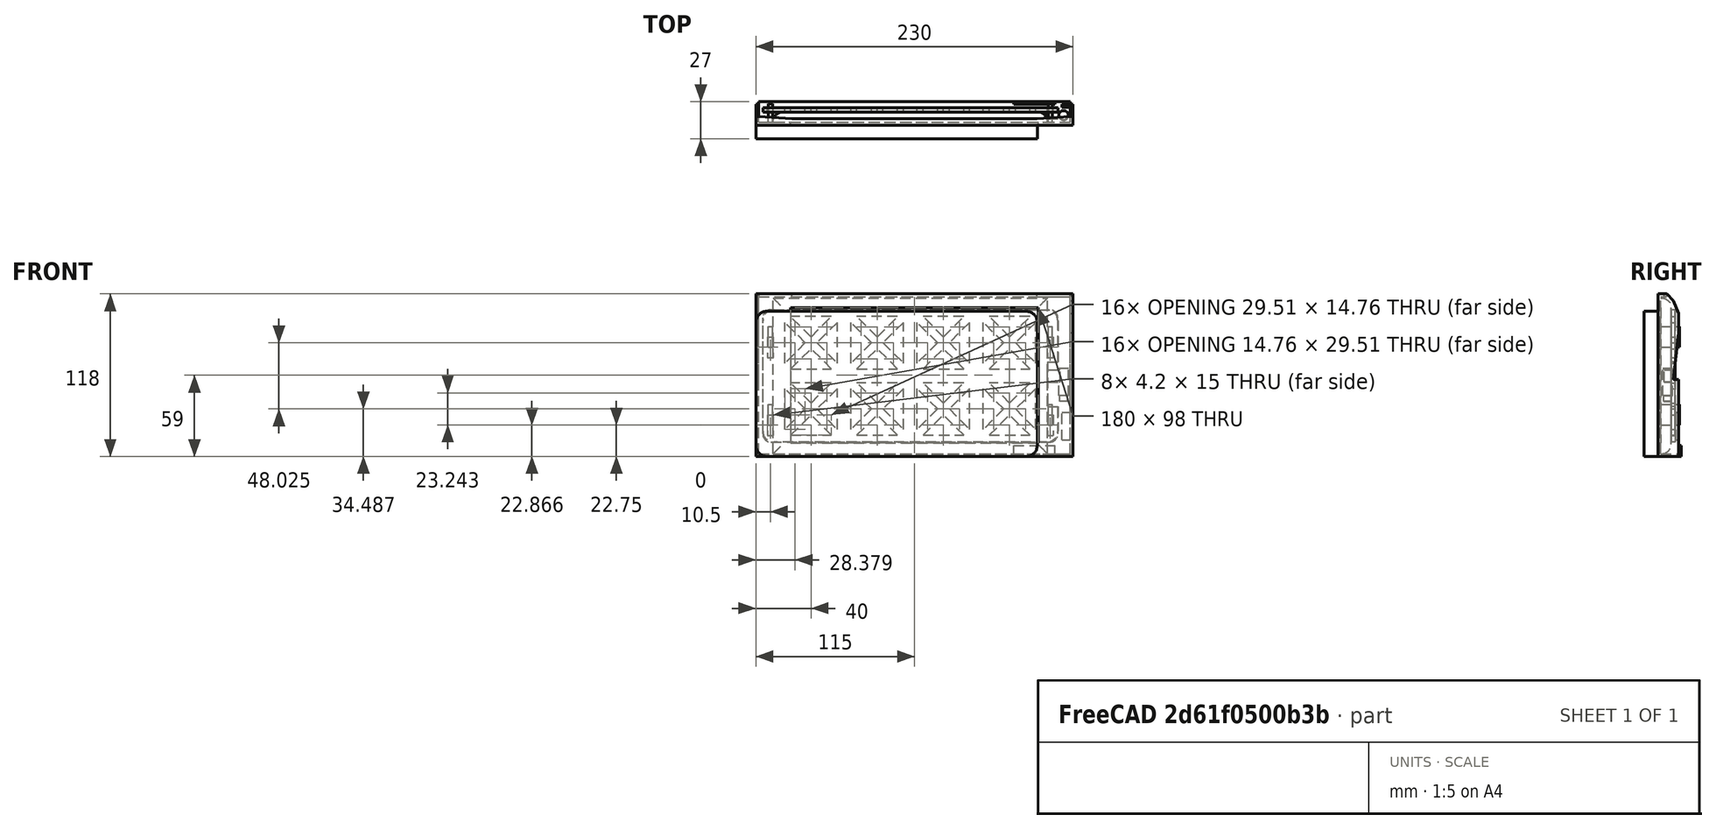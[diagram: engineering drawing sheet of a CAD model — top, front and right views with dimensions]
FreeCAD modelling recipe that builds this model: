
FCSTD DOCUMENT  (FreeCAD 0.18.1R)
Label: case
License: All rights reserved
LicenseURL: http://en.wikipedia.org/wiki/All_rights_reserved
objects: Part::Box×15, Part::Cut×15, Sketcher::SketchObject×7, Part::Extrusion×4, Mesh::Feature×3, Part::Cylinder×2, Part::MultiFuse×2, Part::Fillet×2, PartDesign::LinearPattern×2, App::DocumentObjectGroup×2, Spreadsheet::Sheet×1, PartDesign::Pad×1, PartDesign::Pocket×1, PartDesign::MultiTransform×1, PartDesign::Body×1, Image::ImagePlane×1
note: 55 computed .brp shape members not serialized (recipe doc carries the construction recipe); baked Part::Feature solids carry a one-line shape summary decoded from their .brp

FEATURE [Part::Box] Box  label="Cube"
  AttacherType = Attacher::AttachEngine3D
  Height = 118
  Length = 226
  Placement = pos=(2,0,0) rot=(0,0,1;0rad)
  Width = 2
  expr: Placement.Rotation.Axis.x = 0
  expr: Length = Spreadsheet.avl_width - Spreadsheet.thickness * 2
  expr: Placement.Base.x = Spreadsheet.thickness
  expr: Height = Spreadsheet.thickness * 2 + Spreadsheet.tablet_height + Spreadsheet.tablet_height_margin
  expr: Width = Spreadsheet.thickness
FEATURE [Part::Box] Box001  label="Cube001"
  AttacherType = Attacher::AttachEngine3D
  Height = 98
  Length = 180
  Placement = pos=(25,-17,10) rot=(0,0,1;0rad)
  Width = 34
  expr: Placement.Base.y = -Cube001.Width / 2
  expr: Placement.Base.x = Spreadsheet.case_sides_width
  expr: Placement.Base.z = Spreadsheet.case_bottom_height
  expr: Height = Spreadsheet.thickness * 2 + Spreadsheet.tablet_height + Spreadsheet.tablet_height_margin - Spreadsheet.case_bottom_height - Spreadsheet.case_top_height
  expr: Width = Spreadsheet.case_bottom_depth * 2
  expr: Length = Spreadsheet.avl_width - Spreadsheet.case_sides_width * 2
FEATURE [Part::Cut] Cut  label="Main Frame"
  Base = -> Box
  Tool = -> Box001
FEATURE [Sketcher::SketchObject] Sketch
  MapMode = 2
  Support = -> [Sketch]
  sketch-geometry (6):
    g0: LineSegment StartX=0 StartY=0 StartZ=0 EndX=0 EndY=6.3 EndZ=0
    g1: LineSegment StartX=0 StartY=6.3 StartZ=0 EndX=26 EndY=4.5 EndZ=0
    g2: LineSegment StartX=26 StartY=4.5 StartZ=0 EndX=204 EndY=4.5 EndZ=0
    g3: LineSegment StartX=204 StartY=4.5 StartZ=0 EndX=230 EndY=6.3 EndZ=0
    g4: LineSegment StartX=230 StartY=6.3 StartZ=0 EndX=230 EndY=0 EndZ=0
    g5: LineSegment StartX=230 StartY=0 StartZ=0 EndX=0 EndY=0 EndZ=0
  constraints (18):
    c: PointOnObject(g0,g-1)
    c: Vertical(g0)
    c: Coincident(g0,g1)
    c: Coincident(g1,g2)
    c: Horizontal(g2)
    c: Coincident(g2,g3)
    c: Coincident(g3,g4)
    c: PointOnObject(g4,g-1)
    c: Vertical(g4)
    c: Coincident(g4,g5)
    c: Coincident(g5,g0)
    c: Coincident(g0,g-1)
    c: DistanceX(g5,g5) = 230
    c: DistanceY(g0,g0) = 6.3
    c: Equal(g4,g0)
    c: DistanceX(g2,g3) = 26
    c: DistanceX(g0,g1) = 26
    c: DistanceY(g-1,g1) = 4.5
FEATURE [Part::Extrusion] Extrude  label="Top Thin Beam"
  Base = -> Sketch
  Dir = (0,0,1)
  DirMode = 2
  FaceMakerClass = Part::FaceMakerBullseye
  LengthFwd = 2
  LengthRev = 0
  Placement = pos=(0,0,116) rot=(0,0,1;0rad)
  Solid = true
  Symmetric = false
  expr: LengthFwd = Spreadsheet.thickness
  expr: Placement.Base.z = Spreadsheet.thickness + Spreadsheet.tablet_height + Spreadsheet.tablet_height_margin
FEATURE [Sketcher::SketchObject] Sketch001
  MapMode = 4
  Placement = pos=(0,0,0) rot=(0.57735,0.57735,0.57735;2.0944rad)
  expr: Constraints[15] = Spreadsheet.case_sides_depth
  expr: Constraints[10] = Spreadsheet.case_sides_depth
  expr: Constraints.Height = Spreadsheet.thickness * 2 + Spreadsheet.tablet_height + Spreadsheet.tablet_height_margin
  sketch-geometry (9):
    g0: LineSegment StartX=0 StartY=0 StartZ=0 EndX=15 EndY=0 EndZ=0
    g1: LineSegment StartX=15 StartY=0 StartZ=0 EndX=15 EndY=56 EndZ=0
    g2: LineSegment StartX=15 StartY=56 StartZ=0 EndX=11 EndY=56 EndZ=0
    g3: LineSegment StartX=11 StartY=56 StartZ=0 EndX=15 EndY=90 EndZ=0
    g4: LineSegment StartX=15 StartY=90 StartZ=0 EndX=15 EndY=104 EndZ=0
    g5: LineSegment StartX=15 StartY=104 StartZ=0 EndX=11 EndY=113 EndZ=0
    g6: LineSegment StartX=11 StartY=113 StartZ=0 EndX=6.3 EndY=118 EndZ=0
    g7: LineSegment StartX=0 StartY=118 StartZ=0 EndX=0 EndY=0 EndZ=0
    g8: LineSegment StartX=0 StartY=118 StartZ=0 EndX=6.3 EndY=118 EndZ=0
  constraints (26):
    c: Coincident(g8,g7)
    c: Coincident(g8,g6)
    c: Coincident(g6,g5)
    c: Coincident(g5,g4)
    c: Coincident(g4,g3)
    c: Coincident(g2,g3)
    c: Coincident(g2,g1)
    c: Coincident(g0,g1)
    c: Coincident(g0,g-1)
    c: Horizontal(g0)
    c: DistanceX(g0,g0) = 15
    c: Vertical(g1)
    c: DistanceY(g1,g1) = 56
    c: Horizontal(g2)
    c: DistanceX(g2,g2) = 4
    c: DistanceX(g-1,g3) = 15
    c: DistanceY(g-1,g3) = 90
    c: Vertical(g4)
    c: DistanceY(g-1,g4) = 104
    c: DistanceX(g-1,g5) = 11
    c: DistanceY(g-1,g5) = 113
    c: Coincident(g7,g-1)
    c: Vertical(g7)
    c: DistanceY(g7,g7) = 118  'Height'
    c: Horizontal(g8)
    c: DistanceX(g8,g8) = 6.3
FEATURE [Part::Extrusion] Extrude001  label="RightVerticalContour"
  Base = -> Sketch001
  Dir = (1,0,0)
  DirMode = 2
  FaceMakerClass = Part::FaceMakerBullseye
  LengthFwd = 2
  LengthRev = 0
  Placement = pos=(228,0,0) rot=(0,0,1;0rad)
  Solid = true
  Symmetric = false
  expr: LengthFwd = Spreadsheet.B1
  expr: Placement.Base.x = Spreadsheet.B2 - Spreadsheet.B1
FEATURE [Sketcher::SketchObject] Sketch002
  MapMode = 4
  Placement = pos=(0,0,0) rot=(0.57735,0.57735,0.57735;2.0944rad)
  expr: Constraints[15] = Spreadsheet.case_sides_depth
  expr: Constraints[10] = Spreadsheet.case_sides_depth
  expr: Constraints.Height = Sketch001.Constraints.Height
  sketch-geometry (9):
    g0: LineSegment StartX=0 StartY=0 StartZ=0 EndX=15 EndY=0 EndZ=0
    g1: LineSegment StartX=15 StartY=0 StartZ=0 EndX=15 EndY=56 EndZ=0
    g2: LineSegment StartX=15 StartY=56 StartZ=0 EndX=11 EndY=56 EndZ=0
    g3: LineSegment StartX=11 StartY=56 StartZ=0 EndX=15 EndY=90 EndZ=0
    g4: LineSegment StartX=15 StartY=90 StartZ=0 EndX=15 EndY=104 EndZ=0
    g5: LineSegment StartX=15 StartY=104 StartZ=0 EndX=11 EndY=113 EndZ=0
    g6: LineSegment StartX=11 StartY=113 StartZ=0 EndX=6.3 EndY=118 EndZ=0
    g7: LineSegment StartX=0 StartY=118 StartZ=0 EndX=0 EndY=0 EndZ=0
    g8: LineSegment StartX=0 StartY=118 StartZ=0 EndX=6.3 EndY=118 EndZ=0
  constraints (26):
    c: Coincident(g8,g7)
    c: Coincident(g8,g6)
    c: Coincident(g6,g5)
    c: Coincident(g5,g4)
    c: Coincident(g4,g3)
    c: Coincident(g2,g3)
    c: Coincident(g2,g1)
    c: Coincident(g0,g1)
    c: Coincident(g0,g-1)
    c: Horizontal(g0)
    c: DistanceX(g0,g0) = 15
    c: Vertical(g1)
    c: DistanceY(g1,g1) = 56
    c: Horizontal(g2)
    c: DistanceX(g2,g2) = 4
    c: DistanceX(g-1,g3) = 15
    c: DistanceY(g-1,g3) = 90
    c: Vertical(g4)
    c: DistanceY(g-1,g4) = 104
    c: DistanceX(g-1,g5) = 11
    c: DistanceY(g-1,g5) = 113
    c: Coincident(g7,g-1)
    c: Vertical(g7)
    c: DistanceY(g7,g7) = 118  'Height'
    c: Horizontal(g8)
    c: DistanceX(g8,g8) = 6.3
FEATURE [Part::Extrusion] Extrude002  label="LefttVerticalContour"
  Base = -> Sketch002
  Dir = (1,0,0)
  DirMode = 2
  FaceMakerClass = Part::FaceMakerBullseye
  LengthFwd = 2
  LengthRev = 0
  Solid = true
  Symmetric = false
  expr: LengthFwd = Spreadsheet.thickness
FEATURE [Part::Box] Box009  label="Bottom"
  AttacherType = Attacher::AttachEngine3D
  Height = 2
  Length = 226
  Placement = pos=(2,0,0) rot=(0,0,1;0rad)
  Width = 17
  expr: Width = Spreadsheet.case_bottom_depth
  expr: Placement.Base.x = Spreadsheet.thickness
  expr: Height = Spreadsheet.thickness
  expr: Length = Spreadsheet.avl_width - Spreadsheet.thickness * 2
FEATURE [Part::Box] Box010  label="base"
  AttacherType = Attacher::AttachEngine3D
  Height = 15
  Length = 3
  Width = 13.5
  expr: Height = Spreadsheet.back_support_height
  expr: Width = Spreadsheet.tablet_thickness + Spreadsheet.back_thickness * 2
  expr: Length = Spreadsheet.back_support_thickness
FEATURE [Spreadsheet::Sheet] Spreadsheet
  cells = A1=thickness; B1(thickness)=2; A2=avl_width; B2(avl_width)=230; A3=tablet_height_margin; B3(tablet_height_margin)=1; A4=tablet_height; B4(tablet_height)=113; A5=tablet_length_margin; B5(tablet_length_margin)=0.5; A6=tablet_length; B6(tablet_length)=199; A7=tablet_thickness; B7(tablet_thickness)=7.5; A8=usb_length; B8(usb_length)=15; A9=back_support_height; B9(back_support_height)=15; A10=back_support_thickness; B10(back_support_thickness)=3; A11=back_height_rel_tablet; B11(back_height_rel_tablet)=0.85; A12=back_thickness; B12(back_thickness)=3; A13=case_sides_depth; B13(case_sides_depth)=15; A14=case_bottom_depth; B14(case_bottom_depth)=17; A15=case_sides_width; B15(case_sides_width)=25; A16=case_bottom_height; B16(case_bottom_height)=10; A17=case_top_height; B17(case_top_height)=10; A18=back_width_offset; B18(back_width_offset)=4; A19=back_corner_radius; B19(back_corner_radius)=8; A20=back_pattern_beam_thickness; B20(back_pattern_beam_thickness)=6; A21=back_pattern_size; B21(back_pattern_size)=44; A22=back_support_opening_inside_margin; B22(back_support_opening_inside_margin)=4; A23=back_pattern_hor_num; B23(back_pattern_hor_num)=4; A24=back_pattern_ver_num; B24(back_pattern_ver_num)=2; A25=back_pattern_linear_pattern_length; B25(back_pattern_linear_pattern_length)==back_length - 2 * (back_support_thickness + back_support_opening_inside_margin + back_width_offset) - back_pattern_size - (back_length - 2 * (back_support_thickness + back_support_opening_inside_margin + back_width_offset) - back_pattern_hor_num * back_pattern_size) / back_pattern_hor_num; A26=back_length; B26(back_length)==Spreadsheet.tablet_length + 2 * Spreadsheet.tablet_length_margin + 2 * Spreadsheet.back_support_thickness + 2 * Spreadsheet.back_width_offset; A27=magnet_width; B27(magnet_width)=6; A28=magnet_length; B28(magnet_length)=8; A29=magnet_thickness; B29(magnet_thickness)=3; A30=back_support_opening_factor; B30(back_support_opening_factor)=1.4
FEATURE [Part::Box] Box011  label="Tablet"
  AttacherType = Attacher::AttachEngine3D
  Height = 113
  Length = 199
  Placement = pos=(12.5,2,2) rot=(0,0,1;0rad)
  Width = 7.5
  expr: Placement.Base.y = Spreadsheet.thickness
  expr: Placement.Base.z = Spreadsheet.thickness
  expr: Height = Spreadsheet.tablet_height
  expr: Width = Spreadsheet.tablet_thickness
  expr: Length = Spreadsheet.tablet_length
FEATURE [Part::Cylinder] Cylinder
  Angle = 360
  AttacherType = Attacher::AttachEngine3D
  Height = 20
  Placement = pos=(11.75,2.5,-10) rot=(0,0,1;0rad)
  Radius = 3.5
  expr: Placement.Base.z = Cube010.Placement.Base.z - Cylinder.Height / 2
  expr: Placement.Base.y = Cube010.Placement.Base.y + Cube010.Width / 2
  expr: Placement.Base.x = Cube010.Placement.Base.x + Cube010.Length + Cylinder.Radius / 2
FEATURE [Part::Cylinder] Cylinder001
  Angle = 360
  AttacherType = Attacher::AttachEngine3D
  Height = 4
  Placement = pos=(11.75,2.5,-14) rot=(0,0,1;0rad)
  Radius = 3
  expr: Placement.Base.z = Cylinder.Placement.Base.z - Cylinder001.Height
  expr: Placement.Base.y = Cylinder.Placement.Base.y
  expr: Placement.Base.x = Cylinder.Placement.Base.x
FEATURE [Part::Box] Box012  label="Cube010"
  AttacherType = Attacher::AttachEngine3D
  Height = 9
  Length = 10
  Width = 5
FEATURE [Part::MultiFuse] Fusion001  label="USB"
  Placement = pos=(211.5,4.5,54) rot=(0,0,1;0rad)
  Shapes = -> [Cylinder,Box012,Cylinder001]
  expr: Placement.Base.y = Tablet.Placement.Base.y + Tablet.Width - Cube010.Width
  expr: Placement.Base.x = Tablet.Placement.Base.x + Tablet.Length
  expr: Placement.Base.z = Tablet.Placement.Base.z + Tablet.Height / 2 - Cube010.Height / 2
FEATURE [Part::Box] Box015  label="slot"
  AttacherType = Attacher::AttachEngine3D
  Height = 10
  Length = 10
  Placement = pos=(-3.5,7.5,7.5) rot=(0,0,1;0rad)
  Width = 3
  expr: Placement.Base.z = base.Placement.Base.z + base.Height / 2
  expr: Placement.Base.x = base.Placement.Base.x + base.Length / 2 - slot.Length / 2
  expr: Placement.Base.y = base.Placement.Base.y + Spreadsheet.tablet_thickness * 1mm
  expr: Width = Spreadsheet.back_thickness
FEATURE [Part::Cut] Cut001  label="TopLeftBackSupport"
  Base = -> Box010
  Placement = pos=(9,2,79.25) rot=(0,0,1;0rad)
  Tool = -> Box015
  expr: Placement.Base.y = Tablet.Placement.Base.y
  expr: Placement.Base.x = Tablet.Placement.Base.x - Spreadsheet.back_support_thickness * 1mm - Spreadsheet.tablet_length_margin * 1mm
  expr: Placement.Base.z = Spreadsheet.thickness + Spreadsheet.tablet_height * 3 / 4 - Spreadsheet.back_support_height / 2
FEATURE [Part::Cut] Cut002  label="BottomLeftBackSupport"
  Base = -> Box010
  Placement = pos=(9,2,22.75) rot=(0,0,1;0rad)
  Tool = -> Box015
  expr: Placement.Base.z = Spreadsheet.thickness + Spreadsheet.tablet_height / 4 - Spreadsheet.back_support_height / 2
  expr: Placement.Base.y = Tablet.Placement.Base.y
  expr: Placement.Base.x = Tablet.Placement.Base.x - Spreadsheet.back_support_thickness * 1mm - Spreadsheet.tablet_length_margin * 1mm
FEATURE [Part::Cut] Cut003  label="BottomRightBackSupport"
  Base = -> Box010
  Placement = pos=(212,2,22.75) rot=(0,0,1;0rad)
  Tool = -> Box015
  expr: Placement.Base.x = Tablet.Placement.Base.x + Spreadsheet.tablet_length * 1mm + Spreadsheet.tablet_length_margin * 1mm
  expr: Placement.Base.y = Tablet.Placement.Base.y
  expr: Placement.Base.z = Spreadsheet.thickness + Spreadsheet.tablet_height / 4 - Spreadsheet.back_support_height / 2
FEATURE [Part::Cut] Cut004  label="TopRightBackSupport"
  Base = -> Box010
  Placement = pos=(212,2,79.25) rot=(0,0,1;0rad)
  Tool = -> Box015
  expr: Placement.Base.x = Tablet.Placement.Base.x + Spreadsheet.tablet_length * 1mm + Spreadsheet.tablet_length_margin * 1mm
  expr: Placement.Base.y = Tablet.Placement.Base.y
  expr: Placement.Base.z = Spreadsheet.thickness + Spreadsheet.tablet_height * 3 / 4 - Spreadsheet.back_support_height / 2
FEATURE [Part::Fillet] Fillet  label="Tablet Fillet"
  Base = -> Box011
  Edges = 4 edges r=7: [Edge3,Edge7,Edge11,Edge12]
FEATURE [Part::Box] Box016  label="Back"
  AttacherType = Attacher::AttachEngine3D
  Height = 96.05
  Length = 214
  Placement = pos=(5,9.5,10.475) rot=(0,0,1;0rad)
  Width = 3
  expr: Length = Spreadsheet.back_length
  expr: Placement.Base.z = Tablet.Placement.Base.z + Spreadsheet.tablet_height / 2 * 1mm - Back.Height / 2
  expr: Height = Spreadsheet.tablet_height * Spreadsheet.back_height_rel_tablet
  expr: Placement.Base.y = Tablet.Placement.Base.y + Spreadsheet.tablet_thickness * 1mm
  expr: Placement.Base.x = Tablet.Placement.Base.x - Spreadsheet.tablet_length_margin * 1mm - Spreadsheet.back_support_thickness * 1mm - Spreadsheet.back_width_offset * 1mm
  expr: Width = Spreadsheet.back_thickness
FEATURE [Part::Fillet] Fillet001
  Base = -> Box016
  Edges = 4 edges r=6: [Edge2,Edge4,Edge6,Edge8]
FEATURE [Part::Box] Box017  label="USBOpening"
  AttacherType = Attacher::AttachEngine3D
  Height = 32.4
  Length = 10
  Placement = pos=(211.5,4.5,36.3) rot=(0,0,1;0rad)
  Width = 10
  expr: Placement.Base.y = USB.Placement.Base.y
  expr: Placement.Base.x = USB.Placement.Base.x
  expr: Placement.Base.z = USB.Placement.Base.z - USBOpening.Height / 2 - 1.5mm
  expr: Height = (Cylinder.Height + Cylinder001.Height) * 1.35
  expr: Length = Cube010.Width * 2
FEATURE [Part::Cut] Cut005
  Base = -> Fillet001
  Tool = -> Box017
FEATURE [Part::Box] Box018  label="TRSupportOpening"
  AttacherType = Attacher::AttachEngine3D
  Height = 15
  Length = 4.2
  Placement = pos=(211.4,8,71.75) rot=(0,0,1;0rad)
  Width = 6
  expr: Width = Spreadsheet.back_thickness * 2
  expr: Placement.Base.z = TopRightBackSupport.Placement.Base.z - base.Height / 2
  expr: Height = Spreadsheet.back_support_height
  expr: Placement.Base.y = Back.Placement.Base.y - Back.Width / 2
  expr: Placement.Base.x = TopRightBackSupport.Placement.Base.x - (Length - Spreadsheet.back_support_thickness * 1mm) / 2
  expr: Length = Spreadsheet.back_support_thickness * Spreadsheet.back_support_opening_factor
FEATURE [Part::Box] Box019  label="TLSupportOpening"
  AttacherType = Attacher::AttachEngine3D
  Height = 15
  Length = 4.2
  Placement = pos=(8.4,8,71.75) rot=(0,0,1;0rad)
  Width = 6
  expr: Width = Spreadsheet.back_thickness * 2
  expr: Placement.Base.z = TopLeftBackSupport.Placement.Base.z - base.Height / 2
  expr: Height = Spreadsheet.back_support_height
  expr: Placement.Base.y = Back.Placement.Base.y - Back.Width / 2
  expr: Placement.Base.x = TopLeftBackSupport.Placement.Base.x - (Length - Spreadsheet.back_support_thickness * 1mm) / 2
  expr: Length = Spreadsheet.back_support_thickness * Spreadsheet.back_support_opening_factor
FEATURE [Part::Box] Box020  label="BLSupportOpening"
  AttacherType = Attacher::AttachEngine3D
  Height = 15
  Length = 4.2
  Placement = pos=(8.4,8,15.25) rot=(0,0,1;0rad)
  Width = 6
  expr: Width = Spreadsheet.back_thickness * 2
  expr: Placement.Base.z = BottomLeftBackSupport.Placement.Base.z - base.Height / 2
  expr: Height = Spreadsheet.back_support_height
  expr: Placement.Base.y = Back.Placement.Base.y - Back.Width / 2
  expr: Placement.Base.x = BottomLeftBackSupport.Placement.Base.x - (Length - Spreadsheet.back_support_thickness * 1mm) / 2
  expr: Length = Spreadsheet.back_support_thickness * Spreadsheet.back_support_opening_factor
FEATURE [Part::Box] Box021  label="BRSupportOpening"
  AttacherType = Attacher::AttachEngine3D
  Height = 15
  Length = 4.2
  Placement = pos=(211.4,8,15.25) rot=(0,0,1;0rad)
  Width = 6
  expr: Width = Spreadsheet.back_thickness * 2
  expr: Placement.Base.z = BottomLeftBackSupport.Placement.Base.z - base.Height / 2
  expr: Height = Spreadsheet.back_support_height
  expr: Placement.Base.y = Back.Placement.Base.y - Back.Width / 2
  expr: Placement.Base.x = BottomRightBackSupport.Placement.Base.x - (Length - Spreadsheet.back_support_thickness * 1mm) / 2
  expr: Length = Spreadsheet.back_support_thickness * Spreadsheet.back_support_opening_factor
FEATURE [Part::Cut] Cut006
  Base = -> Cut005
  Tool = -> Box018
FEATURE [Part::Cut] Cut007
  Base = -> Cut006
  Tool = -> Box019
FEATURE [Part::Cut] Cut008
  Base = -> Cut007
  Tool = -> Box020
FEATURE [Part::Cut] Cut009
  Base = -> Cut008
  Tool = -> Box021
FEATURE [Sketcher::SketchObject] Sketch004
  Placement = pos=(0,0,0) rot=(1,0,0;1.5708rad)
  expr: Constraints[15] = Spreadsheet.back_corner_radius
  sketch-geometry (8):
    g0: LineSegment StartX=8 StartY=105.426 StartZ=0 EndX=196.081 EndY=105.426 EndZ=0
    g1: LineSegment StartX=204.081 StartY=97.4257 StartZ=0 EndX=204.081 EndY=8.01541 EndZ=0
    g2: LineSegment StartX=196.081 StartY=0.0154091 StartZ=0 EndX=8 EndY=0.0154091 EndZ=0
    g3: LineSegment StartX=7.1e-15 StartY=8.01541 StartZ=0 EndX=7.1e-15 EndY=97.4257 EndZ=0
    g4: ArcOfCircle CenterX=8 CenterY=97.4257 CenterZ=0 NormalX=0 NormalY=0 NormalZ=1 AngleXU=0 Radius=8 StartAngle=1.5708 EndAngle=3.14159
    g5: ArcOfCircle CenterX=196.081 CenterY=97.4257 CenterZ=0 NormalX=0 NormalY=0 NormalZ=1 AngleXU=0 Radius=8 StartAngle=1.232e-13 EndAngle=1.5708
    g6: ArcOfCircle CenterX=196.081 CenterY=8.01541 CenterZ=0 NormalX=0 NormalY=0 NormalZ=1 AngleXU=0 Radius=8 StartAngle=4.71239 EndAngle=6.28319
    g7: ArcOfCircle CenterX=8 CenterY=8.01541 CenterZ=0 NormalX=0 NormalY=0 NormalZ=1 AngleXU=0 Radius=8 StartAngle=3.14159 EndAngle=4.71239
  constraints (17):
    c: Horizontal(g0)
    c: Horizontal(g2)
    c: Vertical(g1)
    c: Vertical(g3)
    c: Tangent(g0,g4) = 1.5708
    c: Tangent(g3,g4) = 1.5708
    c: Tangent(g0,g5) = 1.5708
    c: Tangent(g1,g5) = 1.5708
    c: Tangent(g1,g6) = 1.5708
    c: Tangent(g2,g6) = 1.5708
    c: Tangent(g2,g7) = 1.5708
    c: Tangent(g3,g7) = 1.5708
    c: Equal(g4,g5)
    c: Equal(g5,g6)
    c: Equal(g7,g6)
    c: Radius(g4) = 8
    c: DistanceX(g3,g-1) = 0
FEATURE [Part::Extrusion] Extrude003
  Base = -> Sketch004
  Dir = (0,-1,2e-16)
  DirMode = 2
  FaceMakerClass = Part::FaceMakerBullseye
  LengthFwd = 10
  LengthRev = 0
  Solid = true
  Symmetric = false
FEATURE [Sketcher::SketchObject] Sketch003
  MapMode = 5
  Placement = pos=(0,-10,2.2e-15) rot=(1,0,0;1.5708rad)
  Support = -> [Extrude003]
  sketch-geometry (12):
    g0: LineSegment StartX=-180.28 StartY=91.8225 StartZ=0 EndX=-189.35 EndY=76.113 EndZ=0
    g1: LineSegment StartX=-185.462 StartY=69.3793 StartZ=0 EndX=-167.322 EndY=69.3793 EndZ=0
    g2: LineSegment StartX=-163.434 StartY=76.113 StartZ=0 EndX=-172.504 EndY=91.8225 EndZ=0
    g3: ArcOfCircle CenterX=-176.392 CenterY=89.5779 CenterZ=0 NormalX=0 NormalY=0 NormalZ=1 AngleXU=0 Radius=4.48917 StartAngle=0.523599 EndAngle=2.61799
    g4: ArcOfCircle CenterX=-185.462 CenterY=73.8684 CenterZ=0 NormalX=0 NormalY=0 NormalZ=1 AngleXU=0 Radius=4.48917 StartAngle=2.61799 EndAngle=4.71239
    g5: ArcOfCircle CenterX=-167.322 CenterY=73.8684 CenterZ=0 NormalX=0 NormalY=0 NormalZ=1 AngleXU=0 Radius=4.48917 StartAngle=4.71239 EndAngle=6.80678
    g6: LineSegment StartX=-185.462 StartY=58.9798 StartZ=0 EndX=-167.322 EndY=58.9798 EndZ=0
    g7: LineSegment StartX=-163.434 StartY=52.246 StartZ=0 EndX=-172.504 EndY=36.5366 EndZ=0
    g8: LineSegment StartX=-180.28 StartY=36.5366 StartZ=0 EndX=-189.35 EndY=52.246 EndZ=0
    g9: ArcOfCircle CenterX=-185.462 CenterY=54.4906 CenterZ=0 NormalX=0 NormalY=0 NormalZ=1 AngleXU=0 Radius=4.48917 StartAngle=1.5708 EndAngle=3.66519
    g10: ArcOfCircle CenterX=-167.322 CenterY=54.4906 CenterZ=0 NormalX=0 NormalY=0 NormalZ=1 AngleXU=0 Radius=4.48917 StartAngle=5.75959 EndAngle=7.85398
    g11: ArcOfCircle CenterX=-176.392 CenterY=38.7812 CenterZ=0 NormalX=0 NormalY=0 NormalZ=1 AngleXU=0 Radius=4.48917 StartAngle=3.66519 EndAngle=5.75959
  constraints (29):
    c: Equal(g0,g2)
    c: Equal(g2,g1)
    c: Horizontal(g1)
    c: Tangent(g0,g3) = -1.5708
    c: Tangent(g2,g3) = -1.5708
    c: Tangent(g0,g4) = -1.5708
    c: Tangent(g1,g4) = -1.5708
    c: Tangent(g1,g5) = -1.5708
    c: Tangent(g2,g5) = -1.5708
    c: Horizontal(g6)
    c: Tangent(g6,g9) = 1.5708
    c: Tangent(g8,g9) = 1.5708
    c: Tangent(g6,g10) = 1.5708
    c: Tangent(g7,g10) = 1.5708
    c: Tangent(g7,g11) = 1.5708
    c: Tangent(g8,g11) = 1.5708
    c: Equal(g8,g0)
    c: Equal(g2,g7)
    c: Equal(g6,g1)
    c: Equal(g8,g6)
    c: Equal(g6,g7)
    c: Equal(g1,g0)
    c: Equal(g0,g2)
    c: Equal(g4,g5)
    c: Equal(g5,g3)
    c: Equal(g9,g10)
    c: Equal(g10,g11)
    c: Equal(g10,g5)
    c: DistanceX(g1,g6) = 0
FEATURE [Sketcher::SketchObject] Sketch005
  MapMode = 5
  Placement = pos=(0,0,0) rot=(1,0,0;1.5708rad)
  Support = -> [XZ_Plane]
  expr: Constraints[13] = Spreadsheet.back_corner_radius
  expr: Constraints.back_height = Spreadsheet.tablet_height * Spreadsheet.back_height_rel_tablet
  expr: Constraints.back_width = Spreadsheet.tablet_length + 2 * Spreadsheet.tablet_length_margin + 2 * Spreadsheet.back_support_thickness + 2 * Spreadsheet.back_width_offset
  sketch-geometry (8):
    g0: LineSegment StartX=-99 StartY=48.025 StartZ=0 EndX=99 EndY=48.025 EndZ=0
    g1: LineSegment StartX=107 StartY=40.025 StartZ=0 EndX=107 EndY=-40.025 EndZ=0
    g2: LineSegment StartX=99 StartY=-48.025 StartZ=0 EndX=-99 EndY=-48.025 EndZ=0
    g3: LineSegment StartX=-107 StartY=-40.025 StartZ=0 EndX=-107 EndY=40.025 EndZ=0
    g4: ArcOfCircle CenterX=-99 CenterY=40.025 CenterZ=0 NormalX=0 NormalY=0 NormalZ=1 AngleXU=0 Radius=8 StartAngle=1.5708 EndAngle=3.14159
    g5: ArcOfCircle CenterX=-99 CenterY=-40.025 CenterZ=0 NormalX=0 NormalY=0 NormalZ=1 AngleXU=0 Radius=8 StartAngle=3.14159 EndAngle=4.71239
    g6: ArcOfCircle CenterX=99 CenterY=-40.025 CenterZ=0 NormalX=0 NormalY=0 NormalZ=1 AngleXU=0 Radius=8 StartAngle=4.71239 EndAngle=6.28319
    g7: ArcOfCircle CenterX=99 CenterY=40.025 CenterZ=0 NormalX=0 NormalY=0 NormalZ=1 AngleXU=0 Radius=8 StartAngle=1.072e-13 EndAngle=1.5708
  constraints (18):
    c: Horizontal(g0)
    c: Vertical(g3)
    c: Tangent(g0,g4) = 1.5708
    c: Tangent(g3,g4) = 1.5708
    c: Tangent(g2,g5) = 1.5708
    c: Tangent(g3,g5) = 1.5708
    c: Tangent(g1,g6) = 1.5708
    c: Tangent(g2,g6) = 1.5708
    c: Tangent(g0,g7) = 1.5708
    c: Tangent(g1,g7) = 1.5708
    c: Equal(g4,g7)
    c: Equal(g7,g6)
    c: Equal(g6,g5)
    c: Radius(g4) = 8
    c: Symmetric(g2,g2,g-2)
    c: Symmetric(g1,g1,g-1)
    c: DistanceX(g3,g1) = 214  'back_width'
    c: DistanceY(g2,g0) = 96.05  'back_height'
FEATURE [PartDesign::Pad] Pad
  Length = 3
  Length2 = 100
  Placement = pos=(0,0,0) rot=(1,0,0;1.5708rad)
  Profile = -> Sketch005
  Type = 0
  expr: Length = Spreadsheet.back_thickness
FEATURE [Sketcher::SketchObject] Sketch006
  MapMode = 5
  Placement = pos=(0,-3,-3.104e-13) rot=(1,0,0;1.5708rad)
  Support = -> [Pad]
  expr: Constraints[68] = Spreadsheet.back_pattern_beam_thickness / 2
  expr: Constraints[67] = Spreadsheet.back_pattern_beam_thickness / 2
  expr: Constraints[59] = Spreadsheet.back_pattern_size / 2
  expr: Constraints[33] = Spreadsheet.back_pattern_size * 1mm + 3 * (Back.Length / 2 - (Spreadsheet.back_support_thickness + Spreadsheet.back_width_offset + Spreadsheet.back_support_opening_inside_margin) * 1mm - 2 * Spreadsheet.back_pattern_size * 1mm) / 4
  expr: Constraints[58] = Spreadsheet.back_pattern_size / 2
  expr: Constraints[31] = Spreadsheet.back_pattern_size
  expr: Constraints[32] = (Back.Height / 2 - Spreadsheet.back_pattern_size * 1mm) / 2
  sketch-geometry (32):
    g0: LineSegment [constr] StartX=-94 StartY=46.0125 StartZ=0 EndX=-50 EndY=46.0125 EndZ=0
    g1: LineSegment [constr] StartX=-50 StartY=46.0125 StartZ=0 EndX=-50 EndY=2.0125 EndZ=0
    g2: LineSegment [constr] StartX=-50 StartY=2.0125 StartZ=0 EndX=-94 EndY=2.0125 EndZ=0
    g3: LineSegment [constr] StartX=-94 StartY=2.0125 StartZ=0 EndX=-94 EndY=46.0125 EndZ=0
    g4: LineSegment [constr] StartX=-94 StartY=46.0125 StartZ=0 EndX=-50 EndY=2.0125 EndZ=0
    g5: LineSegment [constr] StartX=-94 StartY=2.0125 StartZ=0 EndX=-50 EndY=46.0125 EndZ=0
    g6: GeomPoint X=-91 Y=38.7699 Z=0
    g7: GeomPoint X=-91 Y=9.25514 Z=0
    g8: GeomPoint X=-76.2426 Y=24.0125 Z=0
    g9: LineSegment StartX=-91 StartY=38.7699 StartZ=0 EndX=-91 EndY=9.25514 EndZ=0
    g10: LineSegment StartX=-91 StartY=9.25514 StartZ=0 EndX=-76.2426 EndY=24.0125 EndZ=0
    g11: GeomPoint X=-86.7574 Y=43.0125 Z=0
    g12: GeomPoint X=-57.2426 Y=43.0125 Z=0
    g13: GeomPoint X=-72 Y=28.2551 Z=0
    g14: GeomPoint X=-53 Y=38.7699 Z=0
    g15: GeomPoint X=-67.7574 Y=24.0125 Z=0
    g16: GeomPoint X=-53 Y=9.25514 Z=0
    g17: GeomPoint X=-72 Y=19.7699 Z=0
    g18: GeomPoint X=-86.7574 Y=5.0125 Z=0
    g19: GeomPoint X=-57.2426 Y=5.0125 Z=0
    g20: LineSegment StartX=-86.7574 StartY=43.0125 StartZ=0 EndX=-57.2426 EndY=43.0125 EndZ=0
    g21: LineSegment StartX=-57.2426 StartY=43.0125 StartZ=0 EndX=-72 EndY=28.2551 EndZ=0
    g22: LineSegment StartX=-67.7574 StartY=24.0125 StartZ=0 EndX=-53 EndY=38.7699 EndZ=0
    g23: LineSegment StartX=-53 StartY=9.25514 StartZ=0 EndX=-67.7574 EndY=24.0125 EndZ=0
    g24: LineSegment StartX=-72 StartY=19.7699 StartZ=0 EndX=-57.2426 EndY=5.0125 EndZ=0
    g25: LineSegment StartX=-57.2426 StartY=5.0125 StartZ=0 EndX=-86.7574 EndY=5.0125 EndZ=0
    g26: LineSegment StartX=-53 StartY=38.7699 StartZ=0 EndX=-53 EndY=9.25514 EndZ=0
    g27: LineSegment StartX=-91 StartY=38.7699 StartZ=0 EndX=-76.2426 EndY=24.0125 EndZ=0
    g28: LineSegment StartX=-72 StartY=19.7699 StartZ=0 EndX=-86.7574 EndY=5.0125 EndZ=0
    g29: LineSegment StartX=-86.7574 StartY=43.0125 StartZ=0 EndX=-72 EndY=28.2551 EndZ=0
    g30: LineSegment [constr] StartX=-94 StartY=24.0125 StartZ=0 EndX=-50 EndY=24.0125 EndZ=0
    g31: LineSegment [constr] StartX=-72 StartY=46.0125 StartZ=0 EndX=-72 EndY=2.0125 EndZ=0
  constraints (69):
    c: Coincident(g0,g1)
    c: Coincident(g1,g2)
    c: Coincident(g2,g3)
    c: Coincident(g3,g0)
    c: Horizontal(g2)
    c: Vertical(g1)
    c: Vertical(g3)
    c: Coincident(g4,g0)
    c: Coincident(g4,g1)
    c: Coincident(g5,g2)
    c: Coincident(g5,g0)
    c: Equal(g0,g1)
    c: Coincident(g9,g6)
    c: Coincident(g9,g7)
    c: Coincident(g10,g7)
    c: Coincident(g10,g8)
    c: Coincident(g20,g11)
    c: Coincident(g20,g12)
    c: Coincident(g21,g12)
    c: Coincident(g21,g13)
    c: Horizontal(g0)
    c: Coincident(g22,g15)
    c: Coincident(g22,g14)
    c: Coincident(g23,g16)
    c: Coincident(g23,g15)
    c: Coincident(g24,g17)
    c: Coincident(g24,g19)
    c: Coincident(g25,g19)
    c: Coincident(g25,g18)
    c: Coincident(g26,g14)
    c: Coincident(g26,g16)
    c: Distance(g3) = 44
    c: DistanceY(g-1,g1) = 2.0125
    c: DistanceX(g1,g-1) = 50
    c: Coincident(g27,g6)
    c: Coincident(g27,g8)
    c: Coincident(g28,g17)
    c: Coincident(g28,g18)
    c: Coincident(g29,g11)
    c: Coincident(g29,g13)
    c: Horizontal(g20)
    c: Vertical(g26)
    c: Vertical(g9)
    c: Parallel(g22,g5)
    c: Parallel(g21,g5)
    c: Parallel(g29,g4)
    c: Parallel(g27,g4)
    c: Parallel(g10,g5)
    c: Parallel(g28,g5)
    c: Parallel(g24,g4)
    c: Parallel(g23,g4)
    c: Equal(g28,g24)
    c: PointOnObject(g30,g3)
    c: PointOnObject(g30,g1)
    c: Horizontal(g30)
    c: PointOnObject(g31,g0)
    c: PointOnObject(g31,g2)
    c: Vertical(g31)
    c: DistanceY(g30,g0) = 22
    c: DistanceX(g31,g0) = 22
    c: Symmetric(g12,g14,g5)
    c: Symmetric(g11,g6,g4)
    c: Symmetric(g16,g19,g4)
    c: Symmetric(g15,g17,g4)
    c: Symmetric(g14,g16,g30)
    c: Symmetric(g15,g13,g5)
    c: Symmetric(g13,g8,g4)
    c: DistanceY(g2,g18) = 3
    c: Distance(g18,g5) = 3
FEATURE [PartDesign::Pocket] Pocket
  BaseFeature = -> Pad
  Length = 5
  Length2 = 100
  Placement = pos=(0,0,0) rot=(1,0,0;1.5708rad)
  Profile = -> Sketch006
  Type = 1
FEATURE [PartDesign::LinearPattern] LinearPattern
  Direction = -> Sketch006 [H_Axis]
  Length = 144
  Occurrences = 4
  Placement = pos=(0,0,0) rot=(1,0,0;1.5708rad)
  expr: Occurrences = Spreadsheet.back_pattern_hor_num
  expr: Length = Spreadsheet.back_pattern_linear_pattern_length
FEATURE [PartDesign::LinearPattern] LinearPattern001
  Direction = -> Z_Axis
  Length = 48.025
  Occurrences = 2
  Placement = pos=(0,0,0) rot=(1,0,0;1.5708rad)
  Reversed = true
  expr: Length = Back.Height / Spreadsheet.back_pattern_ver_num
  expr: Occurrences = Spreadsheet.back_pattern_ver_num
FEATURE [PartDesign::MultiTransform] MultiTransform
  BaseFeature = -> Pocket
  Originals = -> [Pocket]
  Placement = pos=(0,0,0) rot=(1,0,0;1.5708rad)
  Transformations = -> [LinearPattern,LinearPattern001]
FEATURE [PartDesign::Body] Body
  Group = -> [Sketch005,Pad,Sketch006,Pocket,MultiTransform,LinearPattern,LinearPattern001]
  Origin = -> Origin
  Placement = pos=(112,12.5,58.5) rot=(0,0,1;0rad)
  Tip = -> MultiTransform
  expr: Placement.Base.y = Tablet.Placement.Base.y + Spreadsheet.tablet_thickness * 1mm + Spreadsheet.back_thickness * 1mm
  expr: Placement.Base.x = Back.Placement.Base.x + Back.Length / 2
  expr: Placement.Base.z = Back.Placement.Base.z + Back.Height / 2
FEATURE [Part::Cut] Cut010
  Base = -> Body
  Tool = -> Box017
FEATURE [Part::Cut] Cut011
  Base = -> Cut010
  Tool = -> Box018
FEATURE [Part::Cut] Cut012
  Base = -> Cut011
  Tool = -> Box019
FEATURE [Part::Cut] Cut013
  Base = -> Cut012
  Tool = -> Box020
FEATURE [Part::Cut] Cut014  label="Pocketed Back"
  Base = -> Cut013
  Tool = -> Box021
FEATURE [Image::ImagePlane] ImagePlane
  Placement = pos=(112,0,58.5) rot=(-1,0,0;4.71239rad)
  XSize = 170
  YSize = 90
  expr: Placement.Base.z = ImagePlane.YSize / 2 + Tablet.Placement.Base.y + (Tablet.Height - ImagePlane.YSize) / 2
  expr: Placement.Base.x = ImagePlane.XSize / 2 + Tablet.Placement.Base.x + (Tablet.Length - ImagePlane.XSize) / 2
FEATURE [App::DocumentObjectGroup] Group  label="Tablet Group"
  Group = -> [Fusion001,Fillet,ImagePlane]
FEATURE [Mesh::Feature] Mesh  label="Pocketed Back (Meshed) old"
  Placement = pos=(0,0,0) rot=(1,0,0;1.5708rad)
FEATURE [Part::Box] Box022  label="BottomCableGuard"
  AttacherType = Attacher::AttachEngine3D
  Height = 6
  Length = 30
  Placement = pos=(187,15,2) rot=(0,0,1;0rad)
  Width = 2
  expr: Placement.Base.z = Spreadsheet.thickness
  expr: Placement.Base.x = Bottom.Length - Length - Spreadsheet.magnet_thickness * 3 * 1mm
  expr: Placement.Base.y = Bottom.Placement.Base.y + Bottom.Width - Spreadsheet.thickness * 1mm
  expr: Width = Spreadsheet.thickness
FEATURE [Part::Box] Box023  label="SideCableGuard"
  AttacherType = Attacher::AttachEngine3D
  Height = 20
  Length = 6
  Placement = pos=(222,13,12) rot=(0,0,1;0rad)
  Width = 2
  expr: Placement.Base.z = Spreadsheet.magnet_width * 2
  expr: Placement.Base.y = Spreadsheet.case_sides_depth * 1mm - Width
  expr: Placement.Base.x = RightVerticalContour.Placement.Base.x - Length
  expr: Width = Spreadsheet.thickness
FEATURE [Part::MultiFuse] Fusion
  Refine = true
  Shapes = -> [Cut,Extrude,Extrude001,Extrude002,Box009,Cut001,Cut002,Cut003,Cut004,Box022,Box023]
FEATURE [App::DocumentObjectGroup] Group001  label="Case"
  Group = -> [Fusion]
FEATURE [Mesh::Feature] Mesh002  label="Case (Meshed)"
  Placement = pos=(0,0,0) rot=(1,0,0;1.5708rad)
FEATURE [Mesh::Feature] Mesh003  label="Pocketed Back (Meshed)"
  Placement = pos=(0,0,0) rot=(1,0,0;1.5708rad)
